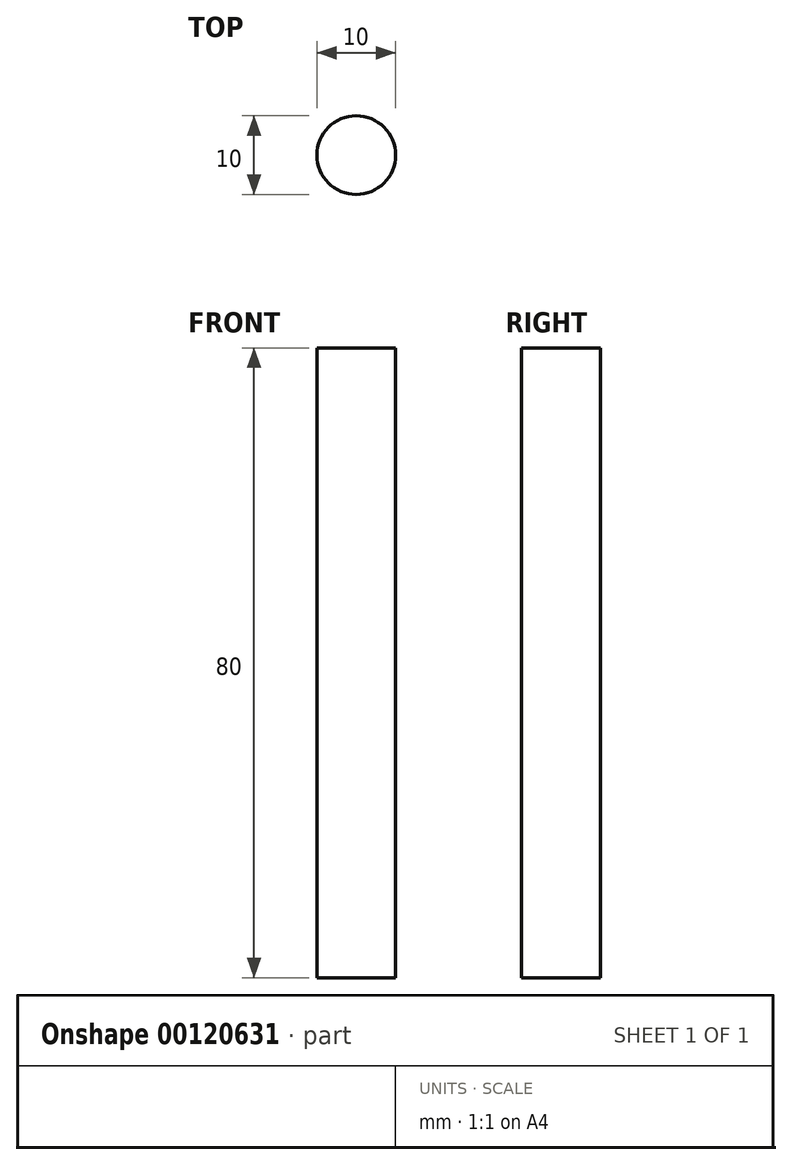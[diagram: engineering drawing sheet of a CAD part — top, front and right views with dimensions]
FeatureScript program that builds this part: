
annotation { "Feature Type Name" : "Feature", "Feature Type Description" : "" }
export const myFeature = defineFeature(function(context is Context, id is Id, definition is map)
    precondition{}
    {
        {
            var Q0;
            Q0=qCreatedBy(makeId("Top.planeOp"),FACE);
            var sketch = newSketch(context, id + "F0", { "sketchPlane" : qUnion([Q0])});
            skCircle(sketch, "E0", {"center": v(0, 0) * mm, "radius": 5 * mm});
            skSolve(sketch);
        }
        {
            var Q0;
            Q0=makeQuery(id+"F0.imprint","IMPRINT",FACE,{"disambiguationData":[TD([[makeQuery(id+"F0.imprint","IMPRINT",EDGE,{"derivedFrom":sQuery(id+"F0.wireOp",EDGE,"E0")}),1.0]])]});
            extrude(context, id + "F1", {"entities" : qUnion([Q0]), "depth" : 80 * mm});
        }
    });
